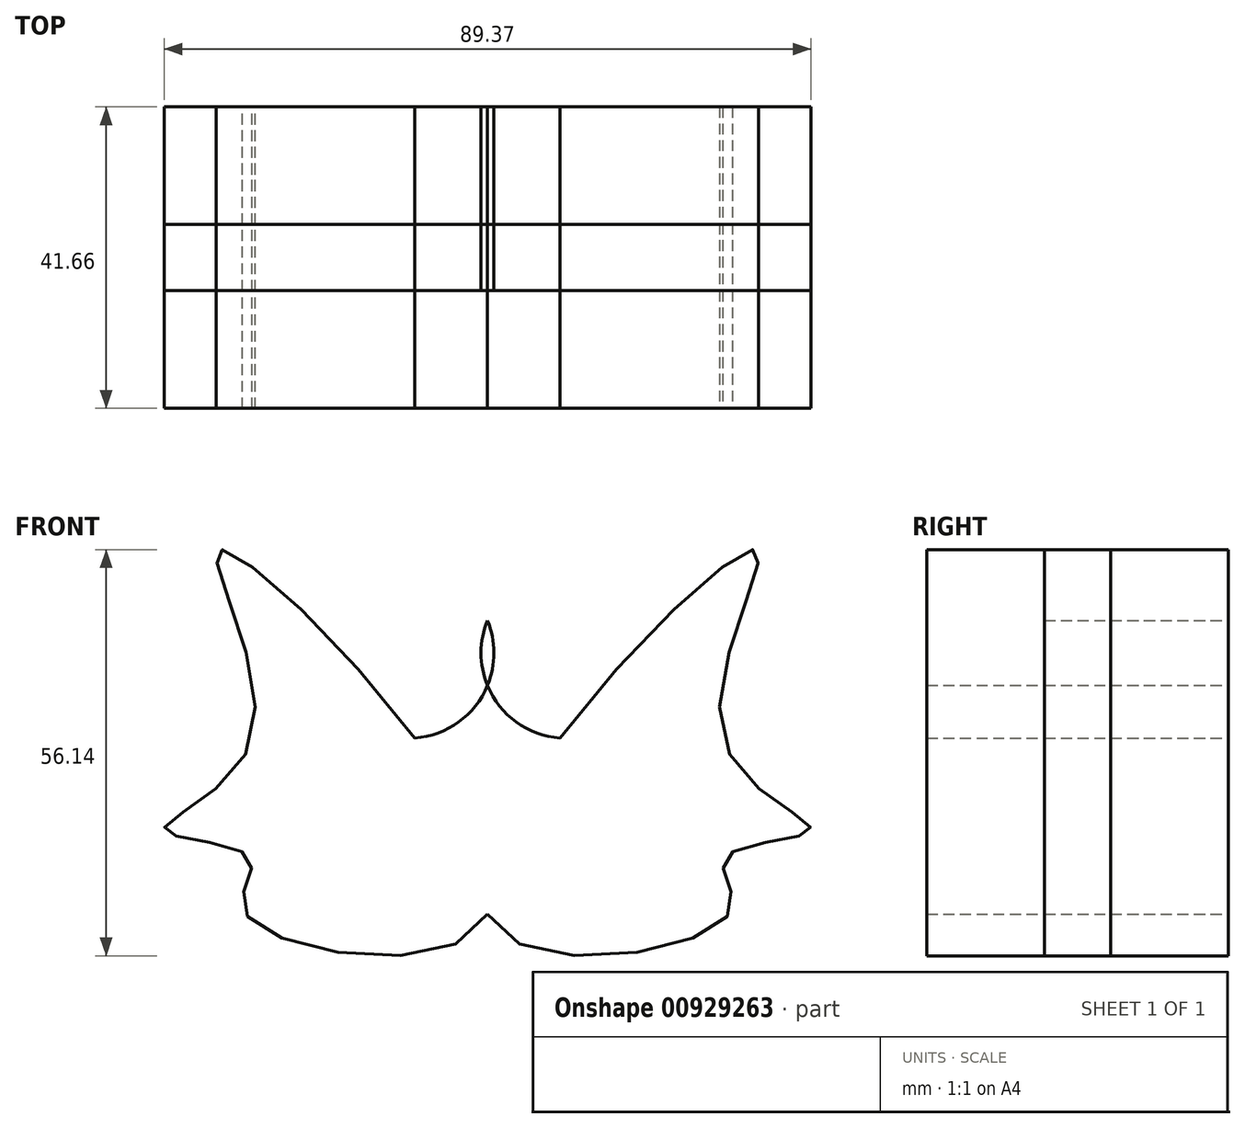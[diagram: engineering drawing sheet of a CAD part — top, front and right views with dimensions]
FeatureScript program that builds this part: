
annotation { "Feature Type Name" : "Feature", "Feature Type Description" : "" }
export const myFeature = defineFeature(function(context is Context, id is Id, definition is map)
    precondition{}
    {
        {
            var Q0;
            Q0=qCreatedBy(makeId("Front.planeOp"),FACE);
            var sketch = newSketch(context, id + "F0", { "sketchPlane" : qUnion([Q0])});
            skLineSegment(sketch, "E0", {"start": v(-17.12, 41.3) * mm, "end": v(-17.12, -24.32) * mm});
            skFitSpline(sketch, "E1", {"points": [v(-53.96, 26.05) * mm, v(-49.65, 0) * mm, v(-61.73, -12.8) * mm, v(-49.93, -16.55) * mm, v(-50.5, -24.32) * mm, v(-17.12, -24.32) * mm, v(-53.96, 26.05) * mm]});
            skFitSpline(sketch, "E2.MirrorC", {"points": [v(19.71, 26.05) * mm, v(15.4, 0) * mm, v(27.49, -12.8) * mm, v(15.69, -16.55) * mm, v(16.26, -24.32) * mm, v(-17.12, -24.32) * mm, v(19.71, 26.05) * mm]});
            skArc(sketch, "E3", {"start": v(-27.16, 0) * mm, "mid": v(-18, 5.57) * mm, "end": v(-17.12, 16.26) * mm});
            skArc(sketch, "E4.MirrorCS", {"start": v(-7.1, 0) * mm, "mid": v(-16.26, 5.57) * mm, "end": v(-17.12, 16.26) * mm});
            skSolve(sketch);
        }
        {
            var Q0;
            Q0 = qSketchRegion(id + "F0", true);
            extrude(context, id + "F1", {"entities" : qUnion([Q0]), "depth" : 25.4 * mm, "offsetDistance" : 25.4 * mm});
        }
        {
            var Q0;
            Q0 = qSketchRegion(id + "F0", true);
            var Q1;
            Q1=makeQuery(id+"F1.opExtrude","CAP_FACE",FACE,{"disambiguationData":[OSD([sQuery(id+"F0.wireOp",EDGE,"E1"),sQuery(id+"F0.wireOp",EDGE,"E2.MirrorC"),sQuery(id+"F0.wireOp",EDGE,"E3"),sQuery(id+"F0.wireOp",EDGE,"E4.MirrorCS")])],"isStart":false});
            extrude(context, id + "F2", {"entities" : qUnion([Q0, Q1]), "depth" : 16.26 * mm, "offsetDistance" : 25.4 * mm});
        }
        {
            var Q0;
            {var subQ0=sQuery(id+"F0.wireOp",EDGE,"E4.MirrorCS");var subQ1=sQuery(id+"F0.wireOp",EDGE,"E3");var subQ2=sQuery(id+"F0.wireOp",EDGE,"E2.MirrorC");var subQ3=sQuery(id+"F0.wireOp",EDGE,"E1");Q0=makeQuery(id+"F2.opExtrude","CAP_FACE",FACE,{"disambiguationData":[OSD([subQ3,subQ2,subQ1,subQ0]),TDD([makeQuery(id+"F1.opExtrude","CAP_FACE",FACE,{"disambiguationData":[OSD([subQ3,subQ2,subQ1,subQ0])],"isStart":false})])],"isStart":false});}
            var sketch = newSketch(context, id + "F3", { "sketchPlane" : qUnion([Q0])});
            skCircle(sketch, "E5", {"center": v(-47.92, -23.74) * mm, "radius": 4.65 * mm});
            skCircle(sketch, "E6", {"center": v(-39.57, -24.32) * mm, "radius": 5.1 * mm});
            skCircle(sketch, "E7", {"center": v(3.3, -24.32) * mm, "radius": 4.5 * mm});
            skCircle(sketch, "E8", {"center": v(11.08, -20.58) * mm, "radius": 4.9 * mm});
            skSolve(sketch);
        }
        {
            var Q0;
            Q0 = qSketchRegion(id + "F3", true);
            extrude(context, id + "F4", {"entities" : qUnion([Q0]), "operationType" : NewBodyOperationType.REMOVE, "depth" : 11.68 * mm, "offsetDistance" : 25.4 * mm});
        }
    });
